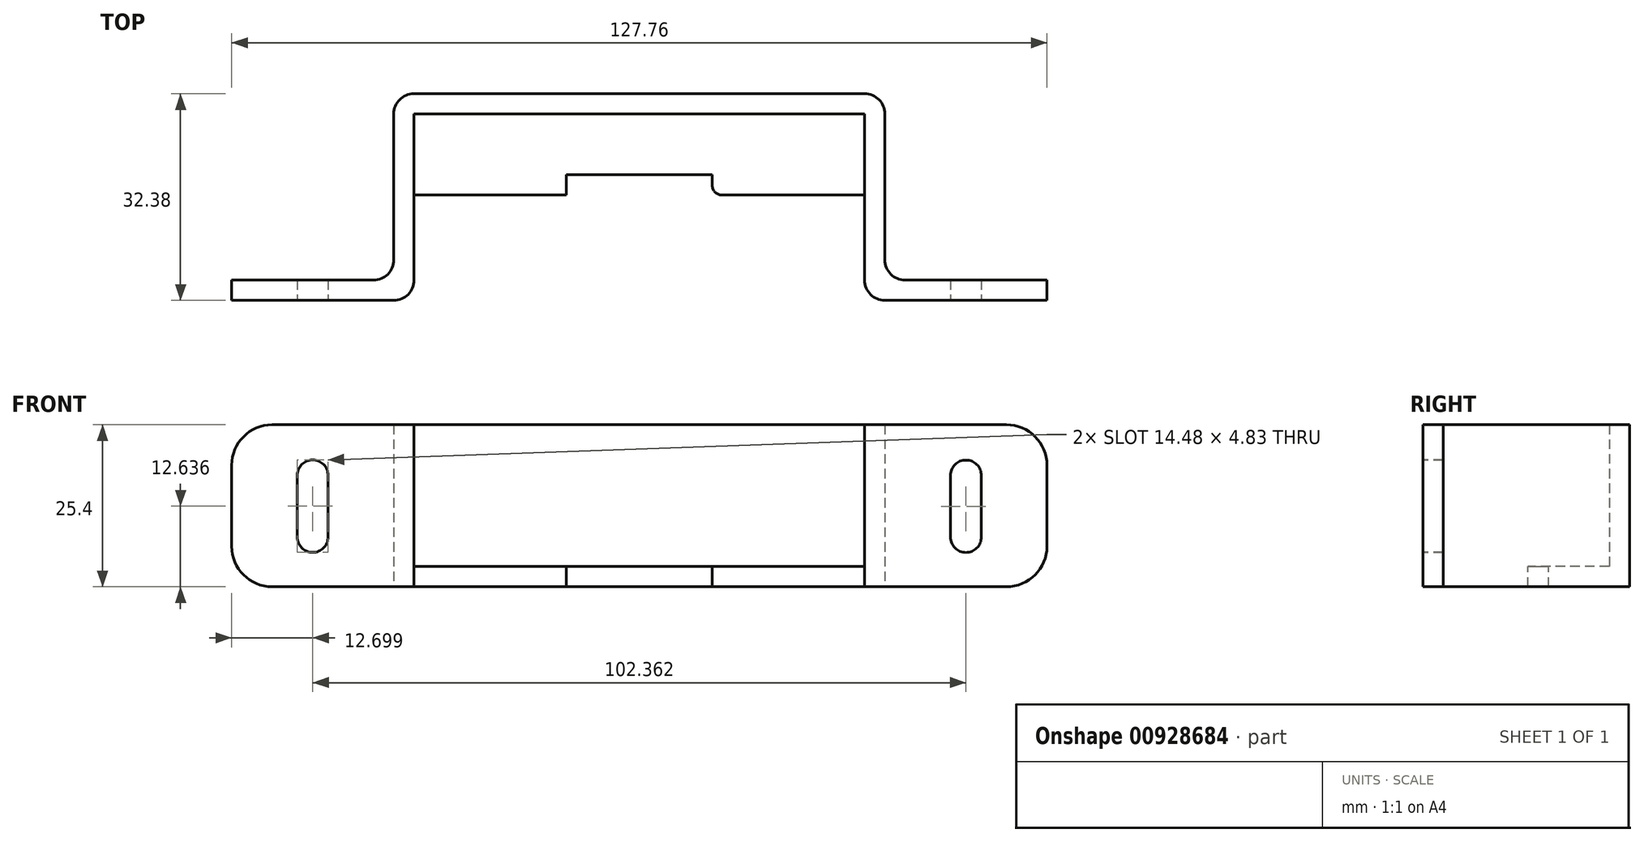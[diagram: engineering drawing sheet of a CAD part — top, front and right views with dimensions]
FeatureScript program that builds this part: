
annotation { "Feature Type Name" : "Feature", "Feature Type Description" : "" }
export const myFeature = defineFeature(function(context is Context, id is Id, definition is map)
    precondition{}
    {
        {
            var Q0;
            Q0=qCreatedBy(makeId("Top.planeOp"),FACE);
            var sketch = newSketch(context, id + "F0", { "sketchPlane" : qUnion([Q0])});
            skLineSegment(sketch, "E0", {"start": v(0, 29.21) * mm, "end": v(35.3, 29.21) * mm});
            skLineSegment(sketch, "E1", {"start": v(35.3, 29.21) * mm, "end": v(35.3, 0) * mm});
            skLineSegment(sketch, "E2", {"start": v(35.3, 0) * mm, "end": v(63.88, 0) * mm});
            skLineSegment(sketch, "E3.0", {"start": v(38.48, 3.17) * mm, "end": v(63.88, 3.17) * mm});
            skLineSegment(sketch, "E3.1", {"start": v(38.48, 32.39) * mm, "end": v(38.48, 3.18) * mm});
            skLineSegment(sketch, "E3.2", {"start": v(0, 32.39) * mm, "end": v(38.48, 32.39) * mm});
            skLineSegment(sketch, "E4", {"start": v(63.88, 3.18) * mm, "end": v(63.88, 0) * mm});
            skLineSegment(sketch, "E5.MirrorCS", {"start": v(-63.88, 3.18) * mm, "end": v(-63.88, 0) * mm});
            skLineSegment(sketch, "E6.MirrorCS", {"start": v(-35.3, 29.21) * mm, "end": v(-35.3, 0) * mm});
            skLineSegment(sketch, "E7.MirrorCS", {"start": v(0, 32.39) * mm, "end": v(-38.48, 32.39) * mm});
            skLineSegment(sketch, "E8.MirrorCS", {"start": v(-38.48, 3.17) * mm, "end": v(-63.88, 3.17) * mm});
            skLineSegment(sketch, "E9.MirrorCS", {"start": v(-35.3, 0) * mm, "end": v(-63.88, 0) * mm});
            skLineSegment(sketch, "E10.MirrorCS", {"start": v(0, 29.21) * mm, "end": v(-35.3, 29.21) * mm});
            skLineSegment(sketch, "E11.MirrorCS", {"start": v(-38.48, 32.39) * mm, "end": v(-38.48, 3.18) * mm});
            skSolve(sketch);
        }
        {
            var Q0;
            Q0 = qSketchRegion(id + "F0", true);
            extrude(context, id + "F1", {"entities" : qUnion([Q0]), "depth" : 25.4 * mm, "offsetDistance" : 25.4 * mm});
        }
        {
            var Q0;
            Q0=makeQuery(id+"F1.opExtrude","SWEPT_EDGE",EDGE,{"disambiguationData":[OSD([sQuery(id+"F0.wireOp",EDGE,"E6.MirrorCS"),sQuery(id+"F0.wireOp",EDGE,"E9.MirrorCS")])]});
            var Q1;
            Q1=makeQuery(id+"F1.opExtrude","SWEPT_EDGE",EDGE,{"disambiguationData":[OSD([sQuery(id+"F0.wireOp",EDGE,"E1"),sQuery(id+"F0.wireOp",EDGE,"E2")])]});
            fillet(context, id + "F2", {"entities" : qUnion([Q0, Q1]), "radius" : 3.17 * mm, "tangentPropagation" : true, "allowEdgeOverflow" : false});
        }
        {
            var Q0;
            Q0=qCreatedBy(makeId("Front.planeOp"),FACE);
            var sketch = newSketch(context, id + "F3", { "sketchPlane" : qUnion([Q0])});
            skLineSegment(sketch, "E12", {"start": v(-51.18, 7.81) * mm, "end": v(-51.18, 17.46) * mm});
            skArc(sketch, "E13.0.startCap", {"start": v(-48.77, 7.81) * mm, "mid": v(-51.18, 5.4) * mm, "end": v(-53.6, 7.81) * mm});
            skArc(sketch, "E13.0.endCap", {"start": v(-53.6, 17.46) * mm, "mid": v(-51.18, 19.88) * mm, "end": v(-48.77, 17.46) * mm});
            skLineSegment(sketch, "E13.0.left", {"start": v(-53.6, 7.81) * mm, "end": v(-53.6, 17.46) * mm});
            skLineSegment(sketch, "E13.0.right", {"start": v(-48.77, 7.81) * mm, "end": v(-48.77, 17.46) * mm});
            skLineSegment(sketch, "E14", {"start": v(51.18, 17.45) * mm, "end": v(51.18, 7.8) * mm});
            skArc(sketch, "E15.0.startCap", {"start": v(48.77, 17.45) * mm, "mid": v(51.18, 19.86) * mm, "end": v(53.6, 17.45) * mm});
            skArc(sketch, "E15.0.endCap", {"start": v(53.6, 7.8) * mm, "mid": v(51.18, 5.38) * mm, "end": v(48.77, 7.8) * mm});
            skLineSegment(sketch, "E15.0.left", {"start": v(53.6, 17.45) * mm, "end": v(53.6, 7.8) * mm});
            skLineSegment(sketch, "E15.0.right", {"start": v(48.77, 17.45) * mm, "end": v(48.77, 7.8) * mm});
            skSolve(sketch);
        }
        {
            var Q0;
            Q0 = qSketchRegion(id + "F3", true);
            extrude(context, id + "F4", {"entities" : qUnion([Q0]), "operationType" : NewBodyOperationType.REMOVE, "endBound" : BoundingType.THROUGH_ALL, "oppositeDirection" : true, "depth" : 25.4 * mm, "offsetDistance" : 25.4 * mm});
        }
        {
            var Q0;
            Q0=makeQuery(id+"F1.opExtrude","CAP_EDGE",EDGE,{"disambiguationData":[OSD([sQuery(id+"F0.wireOp",EDGE,"E5.MirrorCS")])],"isStart":true});
            var Q1;
            Q1=makeQuery(id+"F1.opExtrude","CAP_EDGE",EDGE,{"disambiguationData":[OSD([sQuery(id+"F0.wireOp",EDGE,"E5.MirrorCS")])],"isStart":false});
            var Q2;
            Q2=makeQuery(id+"F1.opExtrude","CAP_EDGE",EDGE,{"disambiguationData":[OSD([sQuery(id+"F0.wireOp",EDGE,"E4")])],"isStart":false});
            var Q3;
            Q3=makeQuery(id+"F1.opExtrude","CAP_EDGE",EDGE,{"disambiguationData":[OSD([sQuery(id+"F0.wireOp",EDGE,"E4")])],"isStart":true});
            fillet(context, id + "F5", {"entities" : qUnion([Q0, Q1, Q2, Q3]), "radius" : 6.35 * mm, "tangentPropagation" : true, "allowEdgeOverflow" : false});
        }
        {
            var Q0;
            Q0=makeQuery(id+"F1.opExtrude","CAP_FACE",FACE,{"disambiguationData":[OSD([sQuery(id+"F0.wireOp",EDGE,"E0"),sQuery(id+"F0.wireOp",EDGE,"E1"),sQuery(id+"F0.wireOp",EDGE,"E2"),sQuery(id+"F0.wireOp",EDGE,"E3.0"),sQuery(id+"F0.wireOp",EDGE,"E3.1"),sQuery(id+"F0.wireOp",EDGE,"E3.2"),sQuery(id+"F0.wireOp",EDGE,"E4"),sQuery(id+"F0.wireOp",EDGE,"E5.MirrorCS"),sQuery(id+"F0.wireOp",EDGE,"E6.MirrorCS"),sQuery(id+"F0.wireOp",EDGE,"E7.MirrorCS"),sQuery(id+"F0.wireOp",EDGE,"E8.MirrorCS"),sQuery(id+"F0.wireOp",EDGE,"E9.MirrorCS"),sQuery(id+"F0.wireOp",EDGE,"E10.MirrorCS"),sQuery(id+"F0.wireOp",EDGE,"E11.MirrorCS")])],"isStart":true});
            var sketch = newSketch(context, id + "F6", { "sketchPlane" : qUnion([Q0])});
            skLineSegment(sketch, "E16.bottom", {"start": v(-35.3, -29.21) * mm, "end": v(35.3, -29.21) * mm});
            skLineSegment(sketch, "E16.top", {"start": v(-35.3, -16.51) * mm, "end": v(35.3, -16.51) * mm});
            skLineSegment(sketch, "E16.left", {"start": v(-35.3, -29.21) * mm, "end": v(-35.3, -16.51) * mm});
            skLineSegment(sketch, "E16.right", {"start": v(35.3, -29.21) * mm, "end": v(35.3, -16.51) * mm});
            skSolve(sketch);
        }
        {
            var Q0;
            Q0 = qSketchRegion(id + "F6", true);
            extrude(context, id + "F7", {"entities" : qUnion([Q0]), "operationType" : NewBodyOperationType.ADD, "oppositeDirection" : true, "depth" : 3.17 * mm, "offsetDistance" : 25.4 * mm});
        }
        {
            var Q0;
            Q0=makeQuery(id+"F1.opExtrude","SWEPT_EDGE",EDGE,{"disambiguationData":[OSD([sQuery(id+"F0.wireOp",EDGE,"E3.0"),sQuery(id+"F0.wireOp",EDGE,"E3.1")])]});
            var Q1;
            Q1=makeQuery(id+"F1.opExtrude","SWEPT_EDGE",EDGE,{"disambiguationData":[OSD([sQuery(id+"F0.wireOp",EDGE,"E3.1"),sQuery(id+"F0.wireOp",EDGE,"E3.2")])]});
            var Q2;
            Q2=makeQuery(id+"F1.opExtrude","SWEPT_EDGE",EDGE,{"disambiguationData":[OSD([sQuery(id+"F0.wireOp",EDGE,"E7.MirrorCS"),sQuery(id+"F0.wireOp",EDGE,"E11.MirrorCS")])]});
            var Q3;
            Q3=makeQuery(id+"F1.opExtrude","SWEPT_EDGE",EDGE,{"disambiguationData":[OSD([sQuery(id+"F0.wireOp",EDGE,"E8.MirrorCS"),sQuery(id+"F0.wireOp",EDGE,"E11.MirrorCS")])]});
            var Q4;
            Q4=makeQuery(id+"F7.opExtrude","SWEPT_EDGE",EDGE,{"disambiguationData":[OSD([sQuery(id+"F0.wireOp",EDGE,"E1"),sQuery(id+"F6.wireOp",EDGE,"E16.top"),sQuery(id+"F6.wireOp",EDGE,"E16.right")])]});
            var Q5;
            Q5=makeQuery(id+"F7.opExtrude","SWEPT_EDGE",EDGE,{"disambiguationData":[OSD([sQuery(id+"F0.wireOp",EDGE,"E6.MirrorCS"),sQuery(id+"F6.wireOp",EDGE,"E16.top"),sQuery(id+"F6.wireOp",EDGE,"E16.left")])]});
            fillet(context, id + "F8", {"entities" : qUnion([Q0, Q1, Q2, Q3, Q4, Q5]), "radius" : 3.17 * mm, "tangentPropagation" : true, "allowEdgeOverflow" : false});
        }
        {
            var Q0;
            Q0=makeQuery(id+"F7.opExtrude","CAP_FACE",FACE,{"disambiguationData":[OSD([sQuery(id+"F6.wireOp",EDGE,"E16.bottom"),sQuery(id+"F6.wireOp",EDGE,"E16.top"),sQuery(id+"F6.wireOp",EDGE,"E16.left"),sQuery(id+"F6.wireOp",EDGE,"E16.right")])],"isStart":false});
            var sketch = newSketch(context, id + "F9", { "sketchPlane" : qUnion([Q0])});
            skLineSegment(sketch, "E17.bottom", {"start": v(-11.43, 16.51) * mm, "end": v(11.43, 16.51) * mm});
            skLineSegment(sketch, "E17.top", {"start": v(-11.43, 19.69) * mm, "end": v(11.43, 19.69) * mm});
            skLineSegment(sketch, "E17.left", {"start": v(-11.43, 16.51) * mm, "end": v(-11.43, 19.69) * mm});
            skLineSegment(sketch, "E17.right", {"start": v(11.43, 16.51) * mm, "end": v(11.43, 19.69) * mm});
            skSolve(sketch);
        }
        {
            var Q0;
            Q0 = qSketchRegion(id + "F9", true);
            extrude(context, id + "F10", {"entities" : qUnion([Q0]), "operationType" : NewBodyOperationType.REMOVE, "oppositeDirection" : true, "depth" : 25.4 * mm, "offsetDistance" : 25.4 * mm});
        }
        {
            var Q0;
            Q0=makeQuery(id+"F10.boolean.opBoolean","COPY",EDGE,{"derivedFrom":makeQuery(id+"F10.opExtrude","SWEPT_EDGE",EDGE,{"disambiguationData":[OSD([sQuery(id+"F6.wireOp",EDGE,"E16.top"),sQuery(id+"F9.wireOp",EDGE,"E17.bottom"),sQuery(id+"F9.wireOp",EDGE,"E17.left")])]})});
            var Q1;
            Q1=makeQuery(id+"F10.boolean.opBoolean","COPY",EDGE,{"derivedFrom":makeQuery(id+"F10.opExtrude","SWEPT_EDGE",EDGE,{"disambiguationData":[OSD([sQuery(id+"F6.wireOp",EDGE,"E16.top"),sQuery(id+"F9.wireOp",EDGE,"E17.bottom"),sQuery(id+"F9.wireOp",EDGE,"E17.right")])]})});
            fillet(context, id + "F11", {"entities" : qUnion([Q0, Q1]), "radius" : 1.52 * mm, "tangentPropagation" : true, "allowEdgeOverflow" : false});
        }
    });
